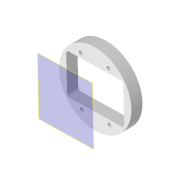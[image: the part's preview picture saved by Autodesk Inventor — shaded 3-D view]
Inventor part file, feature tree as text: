
AUTODESK INVENTOR PART (.ipt)
format: ipt  version: 2022 (Build 260153000, 153)  size: 134,144 bytes
history: native  units: mm
features: reference x3, other x3, plane x1, extrude x1, sketch x1
ambient origin geometry x8: Origin, YZ Plane, XZ Plane, XY Plane, X Axis, Y Axis, Z Axis, Center Point
bodies: Volumenkörper1 (feature_tree)
feature tree (9):
  plane  "Arbeitsebene1"
  extrude  "Extrusion1"  [1 undecoded]
  sketch  "Skizze1"  dims[d0=8.0mm d1=0.0mm]
  reference  "Referenz1"
  reference  "Referenz2"
  reference  "Referenz3"
  other  "<userpath>\Documents\GitHub\Matchboxscope\INVENTOR\Anglerfish_bonne_mamman_m12large_v0.iam"
  other  "Anglerfish_bonne_mamman_m12large_v0.iam"
  other  "Anglerfish_bottom_v0:2"
note: 1 required parameter value undecoded (feature->parameter linkage not recoverable at this tier; creation-order binding heuristic only, values carry confidence <= 0.55)
